# Revit family: 6092_Kunststoffrohranschlüsse G 1_2 für PE-X, PB- & Alu-Verbundrohre (Herz-Ventile der Bau D)
name_source: partatom
category: Rohrformteile
units: mm (PartAtom-declared; Revit-internal decimal feet)

## family parameters
Arbeitsebenenbasiert = Nein
Beim Laden mit Abzugskörper schneiden = Nein
Bemaßung runder Anschluss = Durchmesser verwenden
Gemeinsam genutzt = Nein
Immer vertikal = Ja
OmniClass-Nummer = 23.65.55.14
OmniClass-Titel = Valves for Liquid Services
Teiletyp = Verbindung

## types (1)
- G1/2 x 16x2.0mm
    Anwendungsgebiet = Die Kunststoffrohranschlüsse sind geeignet für Heizungsinstallationen der Anwendungsklassen 1,2, 4 und 5, gemäß ISO 10508, für Rohre aus PE-X (EN ISO 15875) und PE-RT (EN ISO 22391), sowie für Kunststoff-Metall-Verbundrohre (EN ISO 21003).
Die Vorgaben der Rohrhersteller bezüglich Druck und Temperatur sind zu beachten.
Der Kunststoffrohranschluss stellt eine absolut sichere Verbindung zwischen Rohr und Ventilgehäuse dar.
Diese Verbindung kann bei Bedarf jederzeit gelöst werden.
Eine einwandfreie Dichtheit ist auf Dauer nur dann gegeben, wenn die Montage ordnungsgemäß nach HERZ-Montageanleitung durchgeführt wurde.
    Ausführung = 1 6092 01  G1/2 - 16mm:
Klemmset für Kunststoffrohranschluss, bestehend aus Druckschraube und Klemmring, Klemmset G1/2;
passend für Ventileder Baureihe D, TS 7728 (M30x1,5), DELUXE und RL-5.
    Bestellnummer = 1609201
    Hersteller = HERZ Armaturen Ges.m.b.H.
    Hinweiß zum Werkstoff = Gemäß Art 33 der REACH-Verordnung (EG Nr. 1907/2006) sind wir verpflichtet, darauf hinzuweisen, dass der Stoff Blei auf der SVHC-Liste geführt wird und dass alle aus Messing bestehenden Bauteile, die in unseren Erzeugnissen verarbeitet sind, mehr als 0,1 % (w/w) Blei (CAS: 7439-92-1 / EINECS: 231-100-4) enthalten.
Da Blei als Legierungsbestandteil fest gebunden ist, sind keine Expositionen zu erwarten und daher sind keine zusätzlichen Angaben zur sicheren Verwendung notwendig.
    KD00 = 9.15 mm
    KD01 = 8.1 mm  [stored 0.0265748 ft]
    KD02 = 7 mm  [stored 0.0229659 ft]
    KD03 = 6 mm  [stored 0.019685 ft]
    KD04 = 7.5 mm  [stored 0.0246063 ft]
    KL00 = 15.5 mm  [stored 0.050853 ft]
    KL01 = 10.1 mm
    KL02 = 1.1 mm  [stored 0.00360892 ft]
    KL03 = 4.3 mm  [stored 0.0141076 ft]
    Klemmring = CW617N
    MD00 = 12.5 mm  [stored 0.0410105 ft]
    MD01 = 10.5 mm  [stored 0.0344488 ft]
    MD02 = 8.25 mm  [stored 0.0270669 ft]
    ML00 = 18 mm  [stored 0.0590551 ft]
    ML01 = 10.5 mm  [stored 0.0344488 ft]
    ML02 = 14 mm  [stored 0.0459318 ft]
    Max. Betriebsdruck = 1000000.0 Pa
    Max. Betriebstemperatur = 95 °C
    Medium = Heizungswasser nach ÖNORM H5195 oder VDI- Richtlinie 2035.
Die Verwendung von Ethylen- oder Propyleneglykol in einem Mischungsverhältnis 25-50% ist zulässig.
    Mutter = CW617N, G 1/2
    Nennweite = 15 mm  [stored 0.0492126 ft]
    Nennweite_Press = 16 mm  [stored 0.0524934 ft]
    O-Ring = EPDM
    S02 = 5 mm  [stored 0.0164042 ft]
    S03 = 5 mm  [stored 0.0164042 ft]
    SCRNCODE = 07;01;02
    SCRNSEQ = AWI;AWI_TYP="1001";2
    TD00 = 5.95 mm  [stored 0.019521 ft]
    TD01 = 7 mm  [stored 0.0229659 ft]
    TD02 = 4.5 mm  [stored 0.0147638 ft]
    TL00 = 20 mm  [stored 0.0656168 ft]
    TL01 = 5.5 mm  [stored 0.0180446 ft]
    TL02 = 1.2 mm  [stored 0.00393701 ft]
    Tülle = CW617N
    URL = www.herz-armaturen.at
    Vorgabe-Ansicht = 0 mm  [stored 0 ft]

note: [stored X ft] marks values corroborated as IEEE doubles in the binary element streams (Revit-internal decimal feet)
